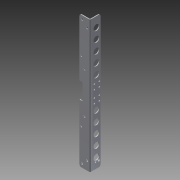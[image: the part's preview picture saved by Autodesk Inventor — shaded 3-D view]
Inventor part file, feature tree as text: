
AUTODESK INVENTOR PART (.ipt)
format: ipt  version: 2014 SP1 (Build 180222100, 222)  size: 340,480 bytes
history: native  units: in
note: dims shown in document units (in); Inventor stores cm internally (conversion verified against a paired STEP export)
features: other x5, reference x5, sketch x4, sheet_metal_op x2, chamfer x1
ambient origin geometry x8: Origin, YZ Plane, XZ Plane, XY Plane, X Axis, Y Axis, Z Axis, Center Point
bodies: Solid1 (feature_tree)
feature tree (17):
  sketch  "Sketch1"  dims[d0=20.0in]
  sheet_metal_op  "Face1"
  sheet_metal_op  "Fold1"
  chamfer  "Corner Round1"
  other  "Plate1"
  sketch  "Sketch2"  dims[d1=3.0in]
  reference  "Reference1"
  reference  "Reference2"
  sketch  "Sketch3"  dims[d2=1.5in]
  reference  "Reference3"
  reference  "Reference4"
  reference  "Reference5"
  sketch  "Sketch4"  dims[d3=0.25in d4=0.01in d5=0.25in d6=11.811in d8=0.6638in d9=0.3937in d11=1.0in d13=0.125in d14=0.125in d15=0.0625in d16=0.25in d17=0.125in d18=90.0deg d19=0.05in d20=0.313in d22=0.75in d23=0.313in d24=0.313in d25=0.375in d26=0.75in d27=0.75in d28=0.55in d29=0.125in d30=0.0in d31=6.2008in d32=0.25in d33=0.5in d34=0.875in d35=0.875in d36=1.5in d37=4.7244in d39=1.5455in d40=0.3937in d42=1.0in d44=0.125in d45=0.0in d46=0.266in d47=0.266in d48=0.25in d49=9.25in d50=0.125in d51=0.0in]
  other  "Cut1"
  other  "Cut2"
  other  "Cut3"
  other  "Definition1"
